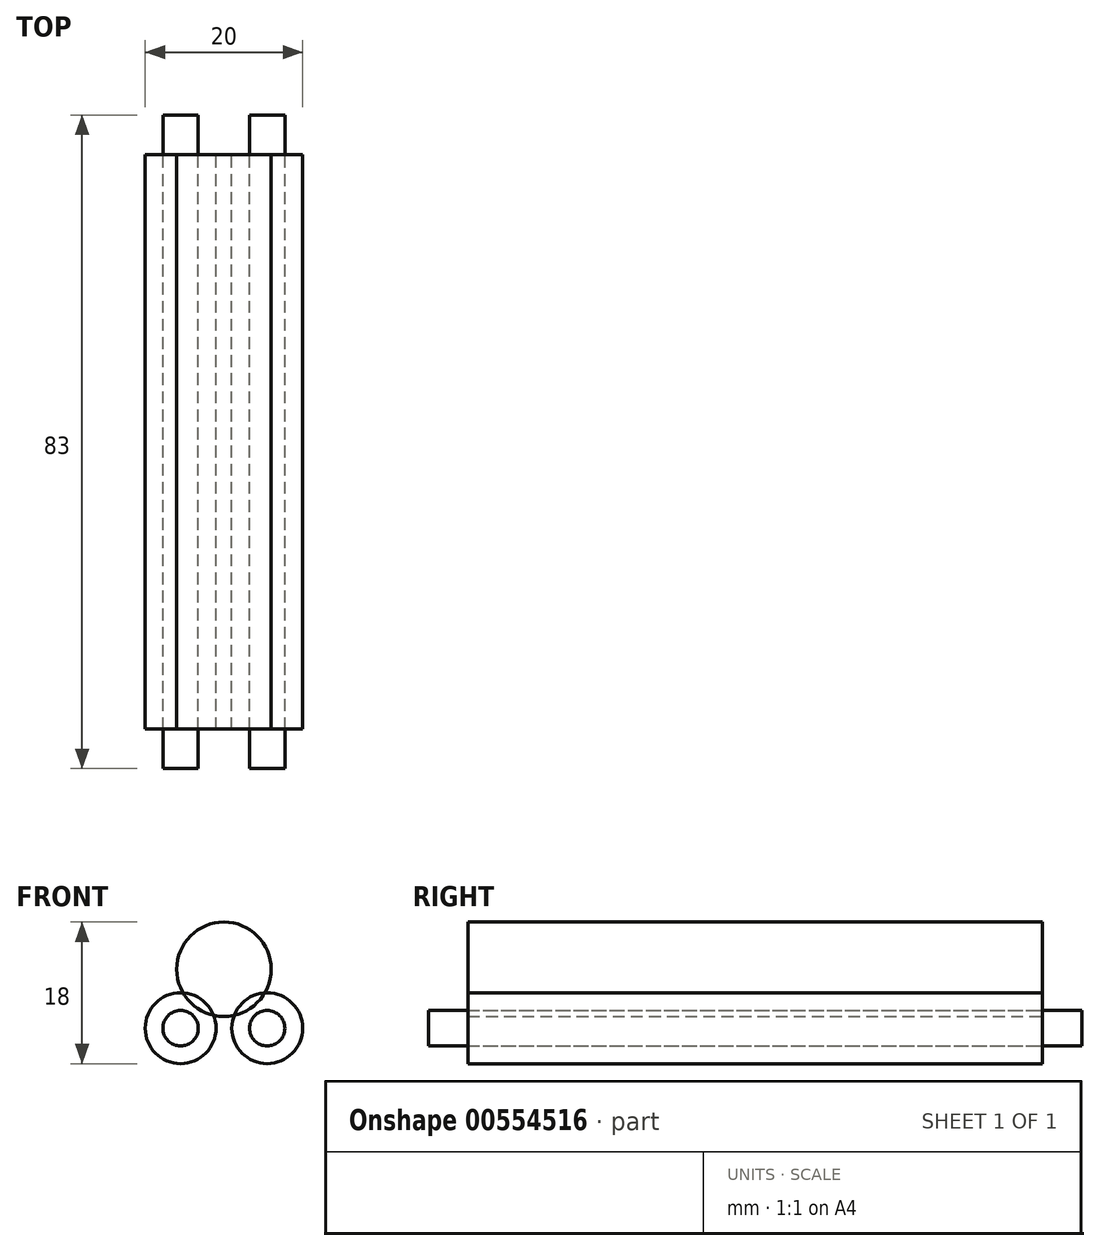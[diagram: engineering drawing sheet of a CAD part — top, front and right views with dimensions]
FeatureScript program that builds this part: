
annotation { "Feature Type Name" : "Feature", "Feature Type Description" : "" }
export const myFeature = defineFeature(function(context is Context, id is Id, definition is map)
    precondition{}
    {
        {
            var Q0;
            Q0=qCreatedBy(makeId("Front.planeOp"),FACE);
            var sketch = newSketch(context, id + "F0", { "sketchPlane" : qUnion([Q0])});
            skLineSegment(sketch, "E0", {"start": v(-5.5, 0) * mm, "end": v(5.5, 0) * mm, "construction": true});
            skCircle(sketch, "E1", {"center": v(-5.5, 0) * mm, "radius": 4.5 * mm});
            skCircle(sketch, "E2", {"center": v(5.5, 0) * mm, "radius": 4.5 * mm});
            skSolve(sketch);
        }
        {
            var Q0;
            Q0 = qSketchRegion(id + "F0", true);
            extrude(context, id + "F1", {"entities" : qUnion([Q0]), "depth" : 36.5 * mm, "offsetDistance" : 25 * mm, "hasSecondDirection" : true, "secondDirectionOppositeDirection" : true, "secondDirectionDepth" : 36.5 * mm});
        }
        {
            var Q0;
            Q0=qCreatedBy(makeId("Front.planeOp"),FACE);
            var sketch = newSketch(context, id + "F2", { "sketchPlane" : qUnion([Q0])});
            skCircle(sketch, "E3", {"center": v(5.5, 0) * mm, "radius": 2.25 * mm});
            skCircle(sketch, "E4", {"center": v(-5.5, 0) * mm, "radius": 2.25 * mm});
            skSolve(sketch);
        }
        {
            var Q0;
            Q0 = qSketchRegion(id + "F2", true);
            extrude(context, id + "F3", {"entities" : qUnion([Q0]), "depth" : 41.5 * mm, "offsetDistance" : 25 * mm, "hasSecondDirection" : true, "secondDirectionOppositeDirection" : true, "secondDirectionDepth" : 41.5 * mm});
        }
        {
            var Q0;
            Q0=qCreatedBy(makeId("Front.planeOp"),FACE);
            var sketch = newSketch(context, id + "F4", { "sketchPlane" : qUnion([Q0])});
            skCircle(sketch, "E5", {"center": v(0, 7.5) * mm, "radius": 6 * mm});
            skSolve(sketch);
        }
        {
            var Q0;
            Q0 = qSketchRegion(id + "F4", true);
            var Q1;
            Q1=makeQuery(id+"F1.opExtrude","CAP_FACE",FACE,{"disambiguationData":[OSD([sQuery(id+"F0.wireOp",EDGE,"E1")])],"isStart":false});
            var Q2;
            Q2=makeQuery(id+"F1.opExtrude","CAP_FACE",FACE,{"disambiguationData":[OSD([sQuery(id+"F0.wireOp",EDGE,"E1")])],"isStart":true});
            extrude(context, id + "F5", {"entities" : qUnion([Q0]), "endBound" : BoundingType.UP_TO_SURFACE, "depth" : 25 * mm, "endBoundEntityFace" : qUnion([Q1]), "offsetDistance" : 25 * mm, "hasSecondDirection" : true, "secondDirectionBound" : SecondDirectionBoundingType.UP_TO_SURFACE, "secondDirectionOppositeDirection" : true, "secondDirectionDepth" : 25 * mm, "secondDirectionBoundEntityFace" : qUnion([Q2])});
        }
    });
